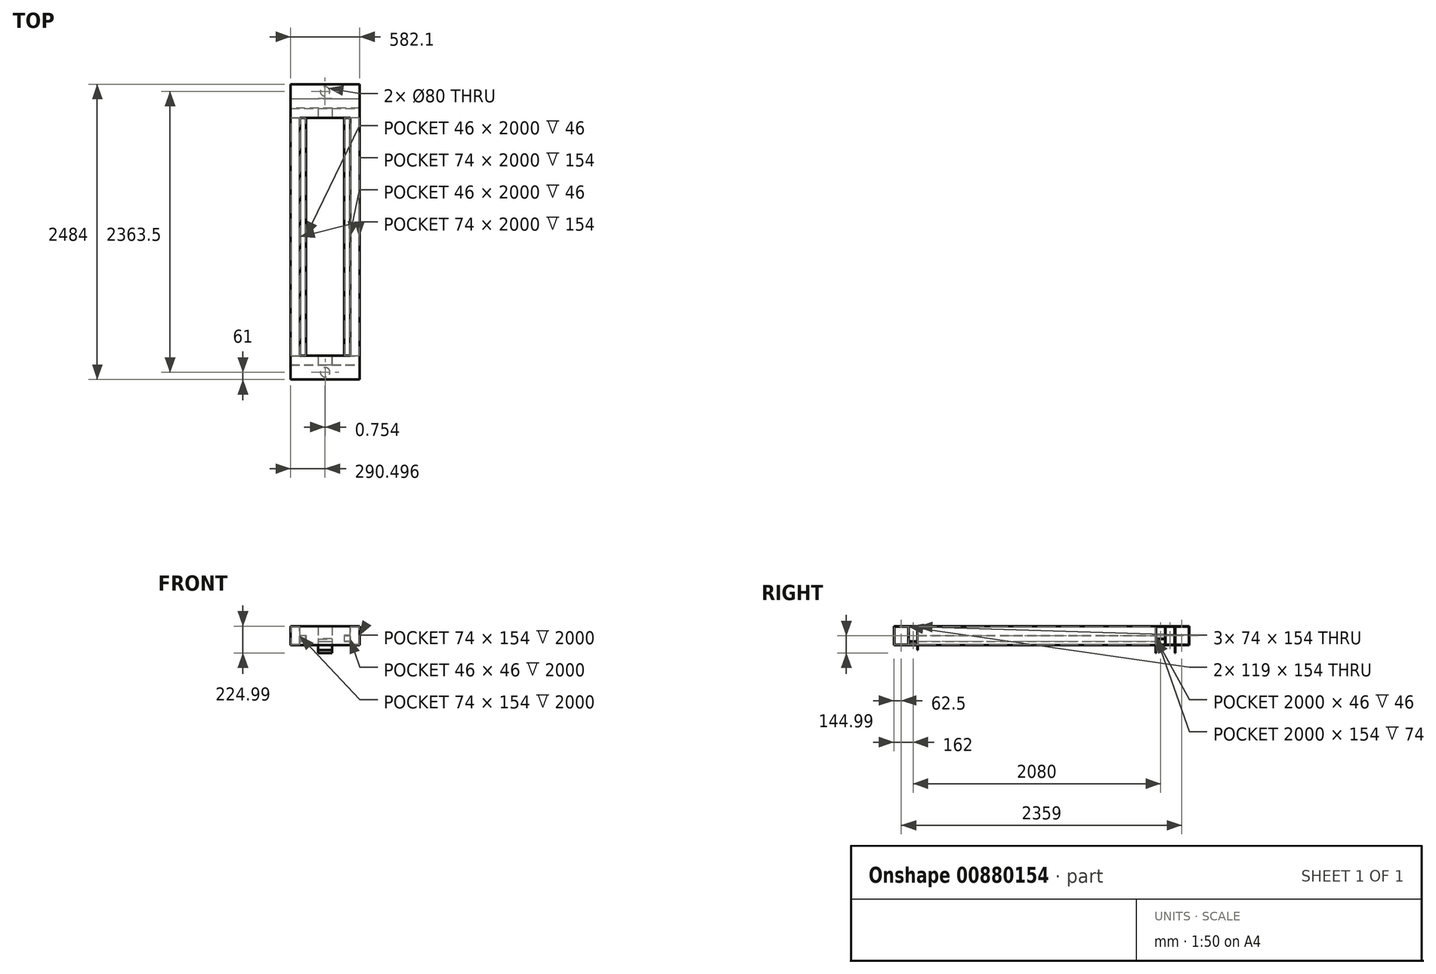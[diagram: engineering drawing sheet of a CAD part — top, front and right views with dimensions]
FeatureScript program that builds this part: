
annotation { "Feature Type Name" : "Feature", "Feature Type Description" : "" }
export const myFeature = defineFeature(function(context is Context, id is Id, definition is map)
    precondition{}
    {
        {
            var Q0;
            Q0=qCreatedBy(makeId("Front.planeOp"),FACE);
            var sketch = newSketch(context, id + "F0", { "sketchPlane" : qUnion([Q0])});
            skLineSegment(sketch, "E0.bottom", {"start": v(0, 0) * mm, "end": v(-80, 0) * mm});
            skLineSegment(sketch, "E0.top", {"start": v(0, 160) * mm, "end": v(-80, 160) * mm});
            skLineSegment(sketch, "E0.left", {"start": v(0, 0) * mm, "end": v(0, 160) * mm});
            skLineSegment(sketch, "E0.right", {"start": v(-80, 0) * mm, "end": v(-80, 160) * mm});
            skLineSegment(sketch, "E1", {"start": v(0, 160) * mm, "end": v(0, 16.85) * mm});
            skLineSegment(sketch, "E2", {"start": v(0, 16.85) * mm, "end": v(0, 81.78) * mm});
            skLineSegment(sketch, "E3", {"start": v(0, 81.78) * mm, "end": v(50, 81.78) * mm});
            skLineSegment(sketch, "E4", {"start": v(50, 81.78) * mm, "end": v(50, 31.78) * mm});
            skLineSegment(sketch, "E5", {"start": v(50, 31.78) * mm, "end": v(0, 31.78) * mm});
            skLineSegment(sketch, "E6", {"start": v(-80, 160) * mm, "end": v(-77, 160) * mm});
            skLineSegment(sketch, "E7", {"start": v(-77, 160) * mm, "end": v(-77, 3) * mm});
            skLineSegment(sketch, "E8", {"start": v(-77, 3) * mm, "end": v(-3, 3) * mm});
            skLineSegment(sketch, "E9", {"start": v(-3, 3) * mm, "end": v(-3, 157) * mm});
            skLineSegment(sketch, "E10", {"start": v(-3, 157) * mm, "end": v(-77, 157) * mm});
            skLineSegment(sketch, "E11", {"start": v(0, 81.78) * mm, "end": v(2, 81.78) * mm});
            skLineSegment(sketch, "E12", {"start": v(2, 81.78) * mm, "end": v(2, 33.78) * mm});
            skLineSegment(sketch, "E13", {"start": v(2, 33.78) * mm, "end": v(48, 33.78) * mm});
            skLineSegment(sketch, "E14", {"start": v(48, 33.78) * mm, "end": v(48, 79.78) * mm});
            skLineSegment(sketch, "E15", {"start": v(48, 79.78) * mm, "end": v(2, 79.78) * mm});
            skSolve(sketch);
        }
        {
            var Q0;
            Q0=makeQuery(id+"F0.imprint","IMPRINT",FACE,{"disambiguationData":[TD([[makeQuery(id+"F0.imprint","IMPRINT",EDGE,{"derivedFrom":sQuery(id+"F0.wireOp",EDGE,"E0.bottom")}),-1.0]])]});
            var Q1;
            Q1=makeQuery(id+"F0.imprint","IMPRINT",FACE,{"disambiguationData":[TD([[makeQuery(id+"F0.imprint","IMPRINT",EDGE,{"derivedFrom":sQuery(id+"F0.wireOp",EDGE,"E3")}),-1.0]])]});
            var Q2;
            Q2 = qSketchRegion(id + "F4", true);
            extrude(context, id + "F1", {"entities" : qUnion([Q0, Q1, Q2]), "depth" : 2000 * mm, "offsetDistance" : 25 * mm});
        }
        {
            var Q0;
            Q0=makeQuery(id+"F1.opExtrude","SWEPT_BODY",BODY,{"disambiguationData":[OSD([sQuery(id+"F0.wireOp",EDGE,"E0.bottom"),sQuery(id+"F0.wireOp",EDGE,"E0.top"),sQuery(id+"F0.wireOp",EDGE,"E0.left"),sQuery(id+"F0.wireOp",EDGE,"E0.right"),sQuery(id+"F0.wireOp",EDGE,"E1"),sQuery(id+"F0.wireOp",EDGE,"E2"),sQuery(id+"F0.wireOp",EDGE,"E3"),sQuery(id+"F0.wireOp",EDGE,"E4"),sQuery(id+"F0.wireOp",EDGE,"E5"),sQuery(id+"F0.wireOp",EDGE,"E6"),sQuery(id+"F0.wireOp",EDGE,"E7"),sQuery(id+"F0.wireOp",EDGE,"E8"),sQuery(id+"F0.wireOp",EDGE,"E9"),sQuery(id+"F0.wireOp",EDGE,"E10"),sQuery(id+"F0.wireOp",EDGE,"E11"),sQuery(id+"F0.wireOp",EDGE,"E12"),sQuery(id+"F0.wireOp",EDGE,"E13"),sQuery(id+"F0.wireOp",EDGE,"E14"),sQuery(id+"F0.wireOp",EDGE,"E15")])]});
            var Q1;
            Q1=makeQuery(id+"F1.opExtrude","SWEPT_FACE",FACE,{"disambiguationData":[OSD([sQuery(id+"F0.wireOp",EDGE,"E4")])]});
            mirror(context, id + "F2", {"entities" : qUnion([Q0]), "mirrorPlane" : qUnion([Q1])});
        }
        {
            var Q0;
            Q0=makeQuery(id+"F2.opPattern","COPY",BODY,{"derivedFrom":makeQuery(id+"F1.opExtrude","SWEPT_BODY",BODY,{"disambiguationData":[OSD([sQuery(id+"F0.wireOp",EDGE,"E0.bottom"),sQuery(id+"F0.wireOp",EDGE,"E0.top"),sQuery(id+"F0.wireOp",EDGE,"E0.left"),sQuery(id+"F0.wireOp",EDGE,"E0.right"),sQuery(id+"F0.wireOp",EDGE,"E1"),sQuery(id+"F0.wireOp",EDGE,"E2"),sQuery(id+"F0.wireOp",EDGE,"E3"),sQuery(id+"F0.wireOp",EDGE,"E4"),sQuery(id+"F0.wireOp",EDGE,"E5"),sQuery(id+"F0.wireOp",EDGE,"E6"),sQuery(id+"F0.wireOp",EDGE,"E7"),sQuery(id+"F0.wireOp",EDGE,"E8"),sQuery(id+"F0.wireOp",EDGE,"E9"),sQuery(id+"F0.wireOp",EDGE,"E10"),sQuery(id+"F0.wireOp",EDGE,"E11"),sQuery(id+"F0.wireOp",EDGE,"E12"),sQuery(id+"F0.wireOp",EDGE,"E13"),sQuery(id+"F0.wireOp",EDGE,"E14"),sQuery(id+"F0.wireOp",EDGE,"E15")])]}),"instanceName":"1"});
            transform(context, id + "F3", {"entities" : qUnion([Q0]), "transformType" : TransformType.TRANSLATION_3D, "dx" : 63 * mm, "dy" : 0 * mm, "dz" : 0 * mm, "makeCopy" : false});
        }
        {
            var Q0;
            Q0=makeQuery(id+"F1.opExtrude","CAP_FACE",FACE,{"disambiguationData":[OSD([sQuery(id+"F0.wireOp",EDGE,"E0.bottom"),sQuery(id+"F0.wireOp",EDGE,"E0.top"),sQuery(id+"F0.wireOp",EDGE,"E0.left"),sQuery(id+"F0.wireOp",EDGE,"E0.right"),sQuery(id+"F0.wireOp",EDGE,"E1"),sQuery(id+"F0.wireOp",EDGE,"E2"),sQuery(id+"F0.wireOp",EDGE,"E3"),sQuery(id+"F0.wireOp",EDGE,"E4"),sQuery(id+"F0.wireOp",EDGE,"E5"),sQuery(id+"F0.wireOp",EDGE,"E6"),sQuery(id+"F0.wireOp",EDGE,"E7"),sQuery(id+"F0.wireOp",EDGE,"E8"),sQuery(id+"F0.wireOp",EDGE,"E9"),sQuery(id+"F0.wireOp",EDGE,"E10"),sQuery(id+"F0.wireOp",EDGE,"E11"),sQuery(id+"F0.wireOp",EDGE,"E12"),sQuery(id+"F0.wireOp",EDGE,"E13"),sQuery(id+"F0.wireOp",EDGE,"E14"),sQuery(id+"F0.wireOp",EDGE,"E15")])],"isStart":false});
            var sketch = newSketch(context, id + "F4", { "sketchPlane" : qUnion([Q0])});
            skLineSegment(sketch, "E16", {"start": v(0, 81.78) * mm, "end": v(412, 81.78) * mm});
            skSolve(sketch);
        }
        {
            var Q0;
            Q0=makeQuery(id+"F2.opPattern","COPY",BODY,{"derivedFrom":makeQuery(id+"F1.opExtrude","SWEPT_BODY",BODY,{"disambiguationData":[OSD([sQuery(id+"F0.wireOp",EDGE,"E0.bottom"),sQuery(id+"F0.wireOp",EDGE,"E0.top"),sQuery(id+"F0.wireOp",EDGE,"E0.left"),sQuery(id+"F0.wireOp",EDGE,"E0.right"),sQuery(id+"F0.wireOp",EDGE,"E1"),sQuery(id+"F0.wireOp",EDGE,"E2"),sQuery(id+"F0.wireOp",EDGE,"E3"),sQuery(id+"F0.wireOp",EDGE,"E4"),sQuery(id+"F0.wireOp",EDGE,"E5"),sQuery(id+"F0.wireOp",EDGE,"E6"),sQuery(id+"F0.wireOp",EDGE,"E7"),sQuery(id+"F0.wireOp",EDGE,"E8"),sQuery(id+"F0.wireOp",EDGE,"E9"),sQuery(id+"F0.wireOp",EDGE,"E10"),sQuery(id+"F0.wireOp",EDGE,"E11"),sQuery(id+"F0.wireOp",EDGE,"E12"),sQuery(id+"F0.wireOp",EDGE,"E13"),sQuery(id+"F0.wireOp",EDGE,"E14"),sQuery(id+"F0.wireOp",EDGE,"E15")])]}),"instanceName":"1"});
            transform(context, id + "F5", {"entities" : qUnion([Q0]), "transformType" : TransformType.TRANSLATION_3D, "dx" : 259.1 * mm, "dy" : 0 * mm, "dz" : 0 * mm, "makeCopy" : false});
        }
        {
            var Q0;
            Q0=makeQuery(id+"F2.opPattern","COPY",FACE,{"derivedFrom":makeQuery(id+"F1.opExtrude","SWEPT_FACE",FACE,{"disambiguationData":[OSD([sQuery(id+"F0.wireOp",EDGE,"E0.right")])]}),"instanceName":"1"});
            var sketch = newSketch(context, id + "F6", { "sketchPlane" : qUnion([Q0])});
            skLineSegment(sketch, "E17", {"start": v(-2000, 160) * mm, "end": v(-2080, 160) * mm});
            skLineSegment(sketch, "E18", {"start": v(-2080, 160) * mm, "end": v(-2080, 0) * mm});
            skLineSegment(sketch, "E19", {"start": v(-2000, 0) * mm, "end": v(-2080, 0) * mm});
            skLineSegment(sketch, "E20", {"start": v(-2080, 160) * mm, "end": v(-2077, 160) * mm});
            skLineSegment(sketch, "E21", {"start": v(-2077, 160) * mm, "end": v(-2077, 3) * mm});
            skLineSegment(sketch, "E22", {"start": v(-2077, 3) * mm, "end": v(-2003, 3) * mm});
            skLineSegment(sketch, "E23", {"start": v(-2003, 3) * mm, "end": v(-2003, 157) * mm});
            skLineSegment(sketch, "E24", {"start": v(-2003, 157) * mm, "end": v(-2077, 157) * mm});
            skSolve(sketch);
        }
        {
            var Q0;
            Q0=makeQuery(id+"F6.imprint","IMPRINT",FACE,{"disambiguationData":[TD([[makeQuery(id+"F6.imprint","IMPRINT",EDGE,{"derivedFrom":sQuery(id+"F6.wireOp",EDGE,"E17")}),1.0]])]});
            extrude(context, id + "F7", {"entities" : qUnion([Q0]), "operationType" : NewBodyOperationType.ADD, "oppositeDirection" : true, "depth" : 582 * mm, "offsetDistance" : 25 * mm});
        }
        {
            var Q0;
            {var subQ0=sQuery(id+"F0.wireOp",EDGE,"E0.right");Q0=makeQuery(id+"F7.boolean.opBoolean","MERGE",FACE,{"derivedFrom":[makeQuery(id+"F2.opPattern","COPY",FACE,{"derivedFrom":makeQuery(id+"F1.opExtrude","SWEPT_FACE",FACE,{"disambiguationData":[OSD([subQ0])]}),"instanceName":"1"}),makeQuery(id+"F7.opExtrude","CAP_FACE",FACE,{"disambiguationData":[OSD([subQ0,sQuery(id+"F6.wireOp",EDGE,"E17"),sQuery(id+"F6.wireOp",EDGE,"E18"),sQuery(id+"F6.wireOp",EDGE,"E19"),sQuery(id+"F6.wireOp",EDGE,"E20"),sQuery(id+"F6.wireOp",EDGE,"E21"),sQuery(id+"F6.wireOp",EDGE,"E22"),sQuery(id+"F6.wireOp",EDGE,"E23"),sQuery(id+"F6.wireOp",EDGE,"E24")])],"isStart":true})]});}
            var sketch = newSketch(context, id + "F8", { "sketchPlane" : qUnion([Q0])});
            skLineSegment(sketch, "E25", {"start": v(0, 160) * mm, "end": v(80, 160) * mm});
            skLineSegment(sketch, "E26", {"start": v(80, 160) * mm, "end": v(80, 0) * mm});
            skLineSegment(sketch, "E27", {"start": v(80, 0) * mm, "end": v(0, 0) * mm});
            skLineSegment(sketch, "E28", {"start": v(0, 0) * mm, "end": v(3, 0) * mm});
            skLineSegment(sketch, "E29", {"start": v(3, 0) * mm, "end": v(3, 157) * mm});
            skLineSegment(sketch, "E30", {"start": v(3, 157) * mm, "end": v(77, 157) * mm});
            skLineSegment(sketch, "E31", {"start": v(77, 157) * mm, "end": v(77, 3) * mm});
            skLineSegment(sketch, "E32", {"start": v(77, 3) * mm, "end": v(3, 3) * mm});
            skSolve(sketch);
        }
        {
            var Q0;
            Q0=makeQuery(id+"F8.imprint","IMPRINT",FACE,{"disambiguationData":[TD([[makeQuery(id+"F8.imprint","IMPRINT",EDGE,{"derivedFrom":sQuery(id+"F8.wireOp",EDGE,"E25")}),-1.0]])]});
            extrude(context, id + "F9", {"entities" : qUnion([Q0]), "operationType" : NewBodyOperationType.ADD, "oppositeDirection" : true, "depth" : 582 * mm, "offsetDistance" : 25 * mm});
        }
        {
            var Q0;
            Q0=makeQuery(id+"F7.opExtrude","SWEPT_FACE",FACE,{"disambiguationData":[OSD([sQuery(id+"F6.wireOp",EDGE,"E18")])]});
            var sketch = newSketch(context, id + "F10", { "sketchPlane" : qUnion([Q0])});
            skLineSegment(sketch, "E33", {"start": v(-79.9, 0) * mm, "end": v(211.25, 0) * mm});
            skLineSegment(sketch, "E34", {"start": v(211.25, 0) * mm, "end": v(211.25, 30.13) * mm});
            skLineSegment(sketch, "E35", {"start": v(211.25, 30.13) * mm, "end": v(153, 30.13) * mm});
            skLineSegment(sketch, "E36", {"start": v(153, 30.13) * mm, "end": v(269.5, 30.13) * mm});
            skLineSegment(sketch, "E37", {"start": v(269.5, 30.13) * mm, "end": v(269.5, 0) * mm});
            skLineSegment(sketch, "E38", {"start": v(153, 30.13) * mm, "end": v(153, 0) * mm});
            skSolve(sketch);
        }
        {
            var Q0;
            Q0 = qSketchRegion(id + "F10", true);
            var Q1;
            {var subQ0=sQuery(id+"F10.wireOp",EDGE,"E34");Q1=makeQuery(id+"F10.imprint","IMPRINT",FACE,{"disambiguationData":[TD([[makeQuery(id+"F10.imprint","IMPRINT",EDGE,{"derivedFrom":subQ0}),-1.0]])]});}
            extrude(context, id + "F11", {"entities" : qUnion([Q0, Q1]), "operationType" : NewBodyOperationType.REMOVE, "endBound" : BoundingType.THROUGH_ALL, "oppositeDirection" : true, "depth" : 90 * mm, "offsetDistance" : 25 * mm});
        }
        {
            var Q0;
            Q0=makeQuery(id+"F7.opExtrude","SWEPT_FACE",FACE,{"disambiguationData":[OSD([sQuery(id+"F6.wireOp",EDGE,"E21")])]});
            var sketch = newSketch(context, id + "F12", { "sketchPlane" : qUnion([Q0])});
            skLineSegment(sketch, "E39", {"start": v(-153, 30.13) * mm, "end": v(-153, 33.13) * mm});
            skLineSegment(sketch, "E40", {"start": v(-153, 33.13) * mm, "end": v(-269.5, 33.13) * mm});
            skLineSegment(sketch, "E41", {"start": v(-269.5, 33.13) * mm, "end": v(-269.5, 30.13) * mm});
            skSolve(sketch);
        }
        {
            var Q0;
            Q0 = qSketchRegion(id + "F12", true);
            var Q1;
            Q1=makeQuery(id+"F12.imprint","IMPRINT",FACE,{"disambiguationData":[TD([[makeQuery(id+"F12.imprint","IMPRINT",EDGE,{"derivedFrom":sQuery(id+"F12.wireOp",EDGE,"E39")}),1.0]])]});
            var Q2;
            Q2 = qSketchRegion(id + "F10", true);
            extrude(context, id + "F13", {"entities" : qUnion([Q0, Q1, Q2]), "operationType" : NewBodyOperationType.ADD, "depth" : 74 * mm, "offsetDistance" : 25 * mm});
        }
        {
            var Q0;
            Q0=makeQuery(id+"F9.opExtrude","SWEPT_FACE",FACE,{"disambiguationData":[OSD([sQuery(id+"F8.wireOp",EDGE,"E31")])]});
            var sketch = newSketch(context, id + "F14", { "sketchPlane" : qUnion([Q0])});
            skLineSegment(sketch, "E42", {"start": v(269.5, 30.13) * mm, "end": v(269.5, 33.13) * mm});
            skLineSegment(sketch, "E43", {"start": v(269.5, 33.13) * mm, "end": v(153, 33.13) * mm});
            skLineSegment(sketch, "E44", {"start": v(153, 33.13) * mm, "end": v(153, 30.13) * mm});
            skSolve(sketch);
        }
        {
            var Q0;
            Q0 = qSketchRegion(id + "F14", true);
            var Q1;
            Q1=makeQuery(id+"F14.imprint","IMPRINT",FACE,{"disambiguationData":[TD([[makeQuery(id+"F14.imprint","IMPRINT",EDGE,{"derivedFrom":sQuery(id+"F14.wireOp",EDGE,"E42")}),1.0]])]});
            extrude(context, id + "F15", {"entities" : qUnion([Q0, Q1]), "operationType" : NewBodyOperationType.ADD, "depth" : 76 * mm, "offsetDistance" : 25 * mm});
        }
        {
            var Q0;
            {var subQ0=sQuery(id+"F10.wireOp",EDGE,"E36");var subQ1=sQuery(id+"F6.wireOp",EDGE,"E21");var subQ4=makeQuery(id+"F11.opExtrude","SWEPT_FACE",FACE,{"disambiguationData":[OSD([subQ0])]});Q0=makeQuery(id+"F13.boolean.opBoolean","MERGE",FACE,{"derivedFrom":[makeQuery(id+"F11.boolean.opBoolean","COPY",FACE,{"disambiguationData":[TD([makeQuery(id+"F7.opExtrude","SWEPT_FACE",FACE,{"disambiguationData":[OSD([sQuery(id+"F6.wireOp",EDGE,"E18")])]})])],"derivedFrom":subQ4}),makeQuery(id+"F11.boolean.opBoolean","COPY",FACE,{"disambiguationData":[TD([makeQuery(id+"F7.opExtrude","SWEPT_FACE",FACE,{"disambiguationData":[OSD([sQuery(id+"F6.wireOp",EDGE,"E23")])]})])],"derivedFrom":subQ4}),makeQuery(id+"F13.opExtrude","SWEPT_FACE",FACE,{"disambiguationData":[OSD([subQ1,subQ0])]})]});}
            var sketch = newSketch(context, id + "F16", { "sketchPlane" : qUnion([Q0])});
            skLineSegment(sketch, "E45", {"start": v(153, 2000) * mm, "end": v(153, 2003) * mm});
            skLineSegment(sketch, "E46", {"start": v(153, 2003) * mm, "end": v(269.5, 2003) * mm});
            skSolve(sketch);
        }
        {
            var Q0;
            Q0 = qSketchRegion(id + "F16", true);
            var Q1;
            Q1=makeQuery(id+"F16.imprint","IMPRINT",FACE,{"disambiguationData":[TD([[makeQuery(id+"F16.imprint","IMPRINT",EDGE,{"derivedFrom":sQuery(id+"F16.wireOp",EDGE,"E45")}),-1.0]])]});
            extrude(context, id + "F17", {"entities" : qUnion([Q0, Q1]), "operationType" : NewBodyOperationType.ADD, "depth" : 71 * mm, "offsetDistance" : 25 * mm});
        }
        {
            var Q0;
            {var subQ0=sQuery(id+"F10.wireOp",EDGE,"E36");var subQ1=sQuery(id+"F8.wireOp",EDGE,"E31");var subQ4=makeQuery(id+"F11.opExtrude","SWEPT_FACE",FACE,{"disambiguationData":[OSD([subQ0])]});Q0=makeQuery(id+"F15.boolean.opBoolean","MERGE",FACE,{"derivedFrom":[makeQuery(id+"F11.boolean.opBoolean","COPY",FACE,{"disambiguationData":[TD([makeQuery(id+"F9.opExtrude","SWEPT_FACE",FACE,{"disambiguationData":[OSD([sQuery(id+"F8.wireOp",EDGE,"E26")])]})])],"derivedFrom":subQ4}),makeQuery(id+"F11.boolean.opBoolean","COPY",FACE,{"disambiguationData":[TD([makeQuery(id+"F9.opExtrude","SWEPT_FACE",FACE,{"disambiguationData":[OSD([sQuery(id+"F8.wireOp",EDGE,"E29")])]})])],"derivedFrom":subQ4}),makeQuery(id+"F15.opExtrude","SWEPT_FACE",FACE,{"disambiguationData":[OSD([subQ1,subQ0])]})]});}
            var sketch = newSketch(context, id + "F18", { "sketchPlane" : qUnion([Q0])});
            skLineSegment(sketch, "E47", {"start": v(269.5, -3) * mm, "end": v(153, -3) * mm});
            skSolve(sketch);
        }
        {
            var Q0;
            Q0 = qSketchRegion(id + "F18", true);
            var Q1;
            Q1=makeQuery(id+"F18.imprint","IMPRINT",FACE,{"disambiguationData":[TD([[makeQuery(id+"F18.imprint","IMPRINT",EDGE,{"derivedFrom":sQuery(id+"F18.wireOp",EDGE,"E47")}),-1.0]])]});
            extrude(context, id + "F19", {"entities" : qUnion([Q0, Q1]), "operationType" : NewBodyOperationType.ADD, "depth" : 95 * mm, "offsetDistance" : 25 * mm});
        }
        {
            var Q0;
            Q0=makeQuery(id+"F9.opExtrude","SWEPT_FACE",FACE,{"disambiguationData":[OSD([sQuery(id+"F8.wireOp",EDGE,"E26")])]});
            var sketch = newSketch(context, id + "F20", { "sketchPlane" : qUnion([Q0])});
            skLineSegment(sketch, "E48", {"start": v(-153, 0) * mm, "end": v(-153, 52.7) * mm});
            skLineSegment(sketch, "E49", {"start": v(-153, 52.7) * mm, "end": v(-269.5, 52.7) * mm});
            skLineSegment(sketch, "E50", {"start": v(-269.5, 52.7) * mm, "end": v(-269.5, 0) * mm});
            skLineSegment(sketch, "E51", {"start": v(-269.5, 52.7) * mm, "end": v(-269.5, 55.7) * mm});
            skLineSegment(sketch, "E52", {"start": v(-269.5, 55.7) * mm, "end": v(-153, 55.7) * mm});
            skLineSegment(sketch, "E53", {"start": v(-153, 55.7) * mm, "end": v(-153, 52.7) * mm});
            skSolve(sketch);
        }
        {
            var Q0;
            Q0 = qSketchRegion(id + "F20", true);
            var Q1;
            {var subQ2=sQuery(id+"F20.wireOp",EDGE,"E49");Q1=makeQuery(id+"F20.imprint","IMPRINT",FACE,{"disambiguationData":[TD([[makeQuery(id+"F20.imprint","IMPRINT",EDGE,{"derivedFrom":subQ2}),1.0]])]});}
            extrude(context, id + "F21", {"entities" : qUnion([Q0, Q1]), "operationType" : NewBodyOperationType.REMOVE, "oppositeDirection" : true, "depth" : 77 * mm, "offsetDistance" : 25 * mm});
        }
        {
            var Q0;
            Q0 = qSketchRegion(id + "F20", true);
            extrude(context, id + "F22", {"entities" : qUnion([Q0]), "operationType" : NewBodyOperationType.ADD, "oppositeDirection" : true, "depth" : 77 * mm, "offsetDistance" : 25 * mm});
        }
        {
            var Q0;
            {var subQ0=sQuery(id+"F10.wireOp",EDGE,"E34");Q0=makeQuery(id+"F10.imprint","IMPRINT",FACE,{"disambiguationData":[TD([[makeQuery(id+"F10.imprint","IMPRINT",EDGE,{"derivedFrom":subQ0}),1.0]])]});}
            extrude(context, id + "F23", {"entities" : qUnion([Q0]), "operationType" : NewBodyOperationType.REMOVE, "oppositeDirection" : true, "depth" : 77 * mm, "offsetDistance" : 25 * mm});
        }
        {
            var Q0;
            Q0=makeQuery(id+"F9.opExtrude","CAP_FACE",FACE,{"disambiguationData":[OSD([sQuery(id+"F0.wireOp",EDGE,"E0.right"),sQuery(id+"F8.wireOp",EDGE,"E25"),sQuery(id+"F8.wireOp",EDGE,"E26"),sQuery(id+"F8.wireOp",EDGE,"E27"),sQuery(id+"F8.wireOp",EDGE,"E28"),sQuery(id+"F8.wireOp",EDGE,"E29"),sQuery(id+"F8.wireOp",EDGE,"E30"),sQuery(id+"F8.wireOp",EDGE,"E31"),sQuery(id+"F8.wireOp",EDGE,"E32")])],"isStart":false});
            var sketch = newSketch(context, id + "F24", { "sketchPlane" : qUnion([Q0])});
            skLineSegment(sketch, "E54", {"start": v(-80, 160) * mm, "end": v(-160, 160) * mm});
            skLineSegment(sketch, "E55", {"start": v(-160, 160) * mm, "end": v(-160, 0) * mm});
            skLineSegment(sketch, "E56", {"start": v(-160, 0) * mm, "end": v(-80, 0) * mm});
            skLineSegment(sketch, "E57", {"start": v(-80, 0) * mm, "end": v(-80, 3) * mm});
            skLineSegment(sketch, "E58", {"start": v(-80, 3) * mm, "end": v(-83, 3) * mm});
            skLineSegment(sketch, "E59", {"start": v(-83, 3) * mm, "end": v(-83, 157) * mm});
            skLineSegment(sketch, "E60", {"start": v(-83, 157) * mm, "end": v(-157, 157) * mm});
            skLineSegment(sketch, "E61", {"start": v(-157, 157) * mm, "end": v(-157, 3) * mm});
            skLineSegment(sketch, "E62", {"start": v(-157, 3) * mm, "end": v(-83, 3) * mm});
            skSolve(sketch);
        }
        {
            var Q0;
            {var subQ1=sQuery(id+"F24.wireOp",EDGE,"E54");Q0=makeQuery(id+"F24.imprint","IMPRINT",FACE,{"disambiguationData":[TD([[makeQuery(id+"F24.imprint","IMPRINT",EDGE,{"derivedFrom":subQ1}),1.0]])]});}
            extrude(context, id + "F25", {"entities" : qUnion([Q0]), "operationType" : NewBodyOperationType.ADD, "oppositeDirection" : true, "depth" : 582 * mm, "offsetDistance" : 25 * mm});
        }
        {
            var Q0;
            Q0=makeQuery(id+"F25.opExtrude","SWEPT_FACE",FACE,{"disambiguationData":[OSD([sQuery(id+"F24.wireOp",EDGE,"E55")])]});
            var sketch = newSketch(context, id + "F26", { "sketchPlane" : qUnion([Q0])});
            skLineSegment(sketch, "E63", {"start": v(-268.75, 0) * mm, "end": v(-268.75, 160) * mm});
            skLineSegment(sketch, "E64", {"start": v(-268.75, 160) * mm, "end": v(-152.25, 160) * mm});
            skLineSegment(sketch, "E65", {"start": v(-152.25, 160) * mm, "end": v(-152.25, -64.99) * mm});
            skLineSegment(sketch, "E66", {"start": v(-152.25, -64.99) * mm, "end": v(-268.75, -64.99) * mm});
            skLineSegment(sketch, "E67", {"start": v(-268.75, 0) * mm, "end": v(-268.75, -64.99) * mm});
            skSolve(sketch);
        }
        {
            var Q0;
            Q0 = qSketchRegion(id + "F26", true);
            extrude(context, id + "F27", {"entities" : qUnion([Q0]), "operationType" : NewBodyOperationType.ADD, "depth" : 3 * mm, "offsetDistance" : 25 * mm});
        }
        {
            var Q0;
            {var subQ0=sQuery(id+"F8.wireOp",EDGE,"E26");var subQ1=sQuery(id+"F0.wireOp",EDGE,"E0.right");Q0=makeQuery(id+"F25.boolean.opBoolean","MERGE",FACE,{"derivedFrom":[makeQuery(id+"F9.boolean.opBoolean","MERGE",FACE,{"derivedFrom":[makeQuery(id+"F7.boolean.opBoolean","MERGE",FACE,{"derivedFrom":[makeQuery(id+"F2.opPattern","COPY",FACE,{"derivedFrom":makeQuery(id+"F1.opExtrude","SWEPT_FACE",FACE,{"disambiguationData":[OSD([subQ1])]}),"instanceName":"1"}),makeQuery(id+"F7.opExtrude","CAP_FACE",FACE,{"disambiguationData":[OSD([subQ1,sQuery(id+"F6.wireOp",EDGE,"E17"),sQuery(id+"F6.wireOp",EDGE,"E18"),sQuery(id+"F6.wireOp",EDGE,"E19"),sQuery(id+"F6.wireOp",EDGE,"E20"),sQuery(id+"F6.wireOp",EDGE,"E21"),sQuery(id+"F6.wireOp",EDGE,"E22"),sQuery(id+"F6.wireOp",EDGE,"E23"),sQuery(id+"F6.wireOp",EDGE,"E24")])],"isStart":true})]}),makeQuery(id+"F9.opExtrude","CAP_FACE",FACE,{"disambiguationData":[OSD([subQ1,sQuery(id+"F8.wireOp",EDGE,"E25"),subQ0,sQuery(id+"F8.wireOp",EDGE,"E27"),sQuery(id+"F8.wireOp",EDGE,"E28"),sQuery(id+"F8.wireOp",EDGE,"E29"),sQuery(id+"F8.wireOp",EDGE,"E30"),sQuery(id+"F8.wireOp",EDGE,"E31"),sQuery(id+"F8.wireOp",EDGE,"E32")])],"isStart":true})]}),makeQuery(id+"F25.opExtrude","CAP_FACE",FACE,{"disambiguationData":[OSD([subQ0,sQuery(id+"F24.wireOp",EDGE,"E54"),sQuery(id+"F24.wireOp",EDGE,"E55"),sQuery(id+"F24.wireOp",EDGE,"E56"),sQuery(id+"F24.wireOp",EDGE,"E57"),sQuery(id+"F24.wireOp",EDGE,"E59"),sQuery(id+"F24.wireOp",EDGE,"E60"),sQuery(id+"F24.wireOp",EDGE,"E61"),sQuery(id+"F24.wireOp",EDGE,"E62")])],"isStart":false})]});}
            var sketch = newSketch(context, id + "F28", { "sketchPlane" : qUnion([Q0])});
            skLineSegment(sketch, "E68", {"start": v(160, 160) * mm, "end": v(282, 160) * mm});
            skLineSegment(sketch, "E69", {"start": v(282, 160) * mm, "end": v(282, 0) * mm});
            skLineSegment(sketch, "E70", {"start": v(282, 0) * mm, "end": v(160, 0) * mm});
            skLineSegment(sketch, "E71", {"start": v(160, 0) * mm, "end": v(160, 3) * mm});
            skLineSegment(sketch, "E72", {"start": v(160, 3) * mm, "end": v(279, 3) * mm});
            skLineSegment(sketch, "E73", {"start": v(279, 3) * mm, "end": v(279, 157) * mm});
            skLineSegment(sketch, "E74", {"start": v(279, 157) * mm, "end": v(160, 157) * mm});
            skLineSegment(sketch, "E75", {"start": v(-2080, 160) * mm, "end": v(-2202, 160) * mm});
            skLineSegment(sketch, "E76", {"start": v(-2202, 160) * mm, "end": v(-2202, 0) * mm});
            skLineSegment(sketch, "E77", {"start": v(-2202, 0) * mm, "end": v(-2080, 0) * mm});
            skLineSegment(sketch, "E78", {"start": v(-2080, 0) * mm, "end": v(-2080, 3) * mm});
            skLineSegment(sketch, "E79", {"start": v(-2080, 3) * mm, "end": v(-2199, 3) * mm});
            skLineSegment(sketch, "E80", {"start": v(-2199, 3) * mm, "end": v(-2199, 157) * mm});
            skLineSegment(sketch, "E81", {"start": v(-2199, 157) * mm, "end": v(-2080, 157) * mm});
            skSolve(sketch);
        }
        {
            var Q0;
            Q0 = qSketchRegion(id + "F28", true);
            var Q1;
            {var subQ0=sQuery(id+"F28.wireOp",EDGE,"E68");Q1=makeQuery(id+"F28.imprint","IMPRINT",FACE,{"disambiguationData":[TD([[makeQuery(id+"F28.imprint","IMPRINT",EDGE,{"derivedFrom":subQ0}),-1.0]])]});}
            extrude(context, id + "F29", {"entities" : qUnion([Q0, Q1]), "operationType" : NewBodyOperationType.ADD, "oppositeDirection" : true, "depth" : 582 * mm, "offsetDistance" : 25 * mm});
        }
        {
            var Q0;
            {var subQ6=sQuery(id+"F8.wireOp",EDGE,"E28");var subQ7=sQuery(id+"F8.wireOp",EDGE,"E27");var subQ9=sQuery(id+"F0.wireOp",EDGE,"E0.right");var subQ16=sQuery(id+"F6.wireOp",EDGE,"E19");var subQ37=sQuery(id+"F0.wireOp",EDGE,"E0.bottom");var subQ40=makeQuery(id+"F1.opExtrude","SWEPT_FACE",FACE,{"disambiguationData":[OSD([subQ9])]});var subQ41=makeQuery(id+"F1.opExtrude","SWEPT_FACE",FACE,{"disambiguationData":[OSD([subQ37])]});var subQ42=makeQuery(id+"F9.boolean.opBoolean","MERGE",FACE,{"derivedFrom":[makeQuery(id+"F7.boolean.opBoolean","MERGE",FACE,{"derivedFrom":[subQ41,makeQuery(id+"F2.opPattern","COPY",FACE,{"derivedFrom":subQ41,"instanceName":"1"}),makeQuery(id+"F7.opExtrude","SWEPT_FACE",FACE,{"disambiguationData":[OSD([subQ16])]})]}),makeQuery(id+"F9.opExtrude","SWEPT_FACE",FACE,{"disambiguationData":[OSD([subQ7,subQ6])]})]});Q0=makeQuery(id+"F29.boolean.opBoolean","MERGE",FACE,{"derivedFrom":[makeQuery(id+"F25.boolean.opBoolean","MERGE",FACE,{"derivedFrom":[makeQuery(id+"F11.boolean.opBoolean","SPLIT",FACE,{"disambiguationData":[TD([makeQuery(id+"F2.opPattern","COPY",FACE,{"derivedFrom":subQ40,"instanceName":"1"})])],"derivedFrom":subQ42}),makeQuery(id+"F13.boolean.opBoolean","MERGE",FACE,{"derivedFrom":[makeQuery(id+"F11.boolean.opBoolean","SPLIT",FACE,{"disambiguationData":[TD([subQ40])],"derivedFrom":subQ42}),makeQuery(id+"F13.opExtrude","SWEPT_FACE",FACE,{"disambiguationData":[OSD([sQuery(id+"F10.wireOp",EDGE,"E33")])]})]}),makeQuery(id+"F25.opExtrude","SWEPT_FACE",FACE,{"disambiguationData":[OSD([sQuery(id+"F24.wireOp",EDGE,"E56")])]})]}),makeQuery(id+"F29.opExtrude","SWEPT_FACE",FACE,{"disambiguationData":[OSD([sQuery(id+"F28.wireOp",EDGE,"E70")])]})]});}
            var sketch = newSketch(context, id + "F30", { "sketchPlane" : qUnion([Q0])});
            skLineSegment(sketch, "E82", {"start": v(210.5, -163) * mm, "end": v(210.5, -282) * mm});
            skLineSegment(sketch, "E83", {"start": v(210.5, -282) * mm, "end": v(210.5, -222.5) * mm});
            skCircle(sketch, "E84", {"center": v(210.5, -222.5) * mm, "radius": 40 * mm});
            skSolve(sketch);
        }
        {
            var Q0;
            Q0 = qSketchRegion(id + "F30", true);
            extrude(context, id + "F31", {"entities" : qUnion([Q0]), "operationType" : NewBodyOperationType.REMOVE, "oppositeDirection" : true, "depth" : 25 * mm, "offsetDistance" : 25 * mm});
        }
        {
            var Q0;
            {var subQ0=sQuery(id+"F28.wireOp",EDGE,"E75");Q0=makeQuery(id+"F28.imprint","IMPRINT",FACE,{"disambiguationData":[TD([[makeQuery(id+"F28.imprint","IMPRINT",EDGE,{"derivedFrom":subQ0}),1.0]])]});}
            extrude(context, id + "F32", {"entities" : qUnion([Q0]), "operationType" : NewBodyOperationType.ADD, "oppositeDirection" : true, "depth" : 582 * mm, "offsetDistance" : 25 * mm});
        }
        {
            var Q0;
            {var subQ6=sQuery(id+"F8.wireOp",EDGE,"E28");var subQ7=sQuery(id+"F8.wireOp",EDGE,"E27");var subQ9=sQuery(id+"F0.wireOp",EDGE,"E0.right");var subQ16=sQuery(id+"F6.wireOp",EDGE,"E19");var subQ37=sQuery(id+"F0.wireOp",EDGE,"E0.bottom");var subQ40=makeQuery(id+"F1.opExtrude","SWEPT_FACE",FACE,{"disambiguationData":[OSD([subQ9])]});var subQ41=makeQuery(id+"F1.opExtrude","SWEPT_FACE",FACE,{"disambiguationData":[OSD([subQ37])]});var subQ42=makeQuery(id+"F9.boolean.opBoolean","MERGE",FACE,{"derivedFrom":[makeQuery(id+"F7.boolean.opBoolean","MERGE",FACE,{"derivedFrom":[subQ41,makeQuery(id+"F2.opPattern","COPY",FACE,{"derivedFrom":subQ41,"instanceName":"1"}),makeQuery(id+"F7.opExtrude","SWEPT_FACE",FACE,{"disambiguationData":[OSD([subQ16])]})]}),makeQuery(id+"F9.opExtrude","SWEPT_FACE",FACE,{"disambiguationData":[OSD([subQ7,subQ6])]})]});Q0=makeQuery(id+"F32.boolean.opBoolean","MERGE",FACE,{"derivedFrom":[makeQuery(id+"F29.boolean.opBoolean","MERGE",FACE,{"derivedFrom":[makeQuery(id+"F25.boolean.opBoolean","MERGE",FACE,{"derivedFrom":[makeQuery(id+"F11.boolean.opBoolean","SPLIT",FACE,{"disambiguationData":[TD([makeQuery(id+"F2.opPattern","COPY",FACE,{"derivedFrom":subQ40,"instanceName":"1"})])],"derivedFrom":subQ42}),makeQuery(id+"F13.boolean.opBoolean","MERGE",FACE,{"derivedFrom":[makeQuery(id+"F11.boolean.opBoolean","SPLIT",FACE,{"disambiguationData":[TD([subQ40])],"derivedFrom":subQ42}),makeQuery(id+"F13.opExtrude","SWEPT_FACE",FACE,{"disambiguationData":[OSD([sQuery(id+"F10.wireOp",EDGE,"E33")])]})]}),makeQuery(id+"F25.opExtrude","SWEPT_FACE",FACE,{"disambiguationData":[OSD([sQuery(id+"F24.wireOp",EDGE,"E56")])]})]}),makeQuery(id+"F29.opExtrude","SWEPT_FACE",FACE,{"disambiguationData":[OSD([sQuery(id+"F28.wireOp",EDGE,"E70")])]})]}),makeQuery(id+"F32.opExtrude","SWEPT_FACE",FACE,{"disambiguationData":[OSD([sQuery(id+"F28.wireOp",EDGE,"E77")])]})]});}
            var sketch = newSketch(context, id + "F33", { "sketchPlane" : qUnion([Q0])});
            skLineSegment(sketch, "E85", {"start": v(211.25, 2080) * mm, "end": v(211.25, 2202) * mm});
            skCircle(sketch, "E86", {"center": v(211.25, 2141) * mm, "radius": 40 * mm});
            skSolve(sketch);
        }
        {
            var Q0;
            Q0 = qSketchRegion(id + "F33", true);
            extrude(context, id + "F34", {"entities" : qUnion([Q0]), "operationType" : NewBodyOperationType.REMOVE, "oppositeDirection" : true, "depth" : 25 * mm, "offsetDistance" : 25 * mm});
        }
    });
